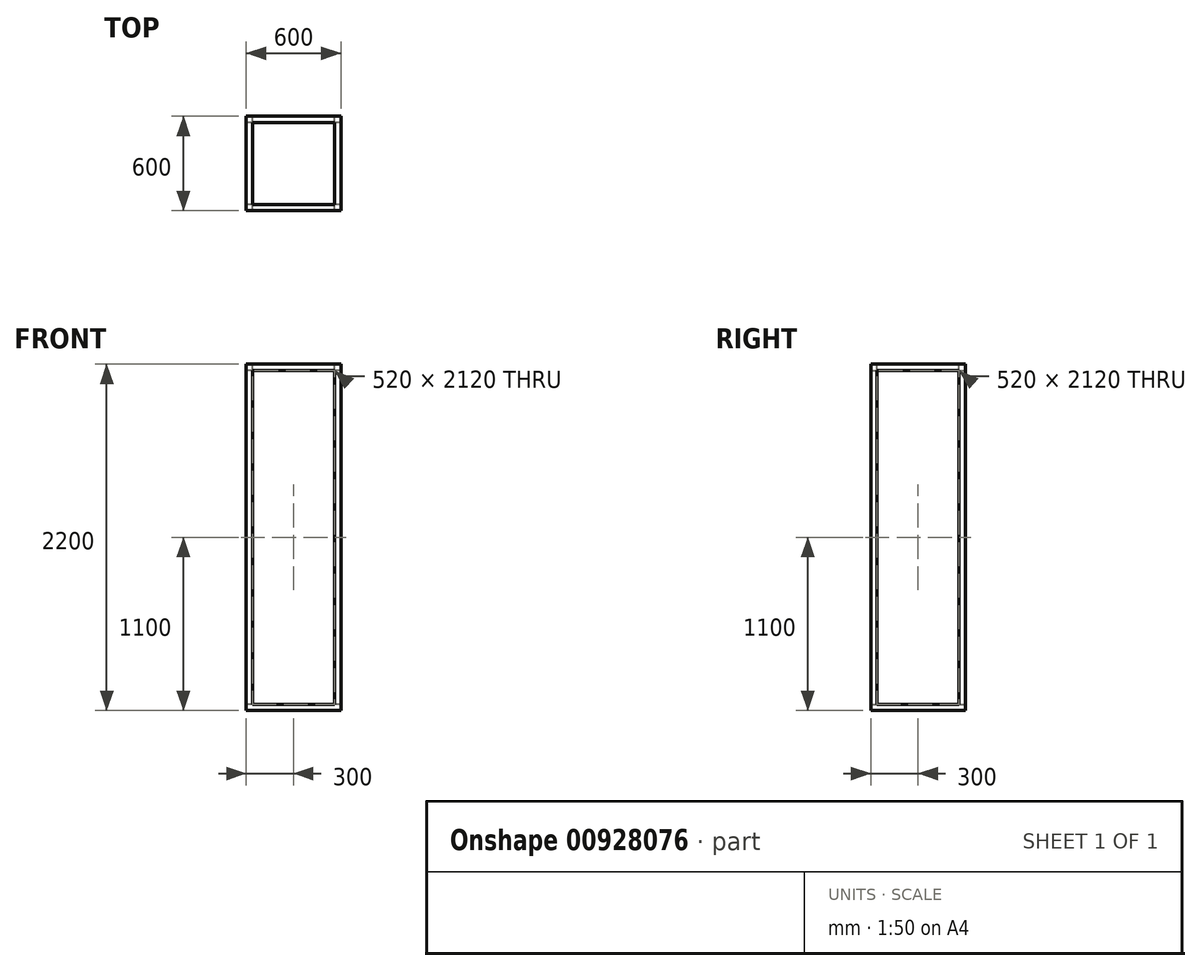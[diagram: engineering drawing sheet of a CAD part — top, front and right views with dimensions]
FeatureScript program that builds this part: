
annotation { "Feature Type Name" : "Feature", "Feature Type Description" : "" }
export const myFeature = defineFeature(function(context is Context, id is Id, definition is map)
    precondition{}
    {
        {
            var Q0;
            Q0=qCreatedBy(makeId("Right.planeOp"),FACE);
            var sketch = newSketch(context, id + "F0", { "sketchPlane" : qUnion([Q0])});
            skLineSegment(sketch, "E0.bottom", {"start": v(-260, -1060) * mm, "end": v(260, -1060) * mm});
            skLineSegment(sketch, "E0.top", {"start": v(-260, 1060) * mm, "end": v(260, 1060) * mm});
            skLineSegment(sketch, "E0.left", {"start": v(-260, -1060) * mm, "end": v(-260, 1060) * mm});
            skLineSegment(sketch, "E0.right", {"start": v(260, -1060) * mm, "end": v(260, 1060) * mm});
            skPoint(sketch, "E0.middle", {"position": v(0, 0) * mm});
            skLineSegment(sketch, "E1.bottom", {"start": v(-300, -1100) * mm, "end": v(300, -1100) * mm});
            skLineSegment(sketch, "E1.top", {"start": v(-300, 1100) * mm, "end": v(300, 1100) * mm});
            skLineSegment(sketch, "E1.left", {"start": v(-300, -1100) * mm, "end": v(-300, 1100) * mm});
            skLineSegment(sketch, "E1.right", {"start": v(300, -1100) * mm, "end": v(300, 1100) * mm});
            skSolve(sketch);
        }
        {
            var Q0;
            Q0=makeQuery(id+"F0.imprint","IMPRINT",FACE,{"disambiguationData":[TD([[makeQuery(id+"F0.imprint","IMPRINT",EDGE,{"derivedFrom":sQuery(id+"F0.wireOp",EDGE,"E0.bottom")}),-1.0]])]});
            extrude(context, id + "F1", {"entities" : qUnion([Q0]), "depth" : 600 * mm, "offsetDistance" : 25 * mm});
        }
        {
            var Q0;
            Q0=makeQuery(id+"F1.opExtrude","SWEPT_FACE",FACE,{"disambiguationData":[OSD([sQuery(id+"F0.wireOp",EDGE,"E1.top")])]});
            var sketch = newSketch(context, id + "F2", { "sketchPlane" : qUnion([Q0])});
            skLineSegment(sketch, "E2.bottom", {"start": v(560, -260) * mm, "end": v(40, -260) * mm});
            skLineSegment(sketch, "E2.top", {"start": v(560, 260) * mm, "end": v(40, 260) * mm});
            skLineSegment(sketch, "E2.left", {"start": v(560, -260) * mm, "end": v(560, 260) * mm});
            skLineSegment(sketch, "E2.right", {"start": v(40, -260) * mm, "end": v(40, 260) * mm});
            skPoint(sketch, "E2.middle", {"position": v(300, 0) * mm});
            skPoint(sketch, "E2.middle.positionSnap0", {"position": v(300, -300) * mm});
            skPoint(sketch, "E2.centerSnap0", {"position": v(300, -300) * mm});
            skSolve(sketch);
        }
        {
            var Q0;
            Q0=makeQuery(id+"F2.imprint","IMPRINT",FACE,{"disambiguationData":[TD([[makeQuery(id+"F2.imprint","IMPRINT",EDGE,{"derivedFrom":sQuery(id+"F2.wireOp",EDGE,"E2.bottom")}),-1.0]])]});
            extrude(context, id + "F3", {"entities" : qUnion([Q0]), "operationType" : NewBodyOperationType.REMOVE, "endBound" : BoundingType.UP_TO_NEXT, "oppositeDirection" : true, "depth" : 25 * mm, "offsetDistance" : 25 * mm});
        }
        {
            var Q0;
            Q0=makeQuery(id+"F1.opExtrude","SWEPT_FACE",FACE,{"disambiguationData":[OSD([sQuery(id+"F0.wireOp",EDGE,"E1.right")])]});
            var sketch = newSketch(context, id + "F4", { "sketchPlane" : qUnion([Q0])});
            skLineSegment(sketch, "E3.bottom", {"start": v(-560, -1060) * mm, "end": v(-40, -1060) * mm});
            skLineSegment(sketch, "E3.top", {"start": v(-560, 1060) * mm, "end": v(-40, 1060) * mm});
            skLineSegment(sketch, "E3.left", {"start": v(-560, -1060) * mm, "end": v(-560, 1060) * mm});
            skLineSegment(sketch, "E3.right", {"start": v(-40, -1060) * mm, "end": v(-40, 1060) * mm});
            skPoint(sketch, "E3.middle", {"position": v(-300, 0) * mm});
            skPoint(sketch, "E3.middle.positionSnap0", {"position": v(-300, -1100) * mm});
            skPoint(sketch, "E3.centerSnap0", {"position": v(-300, -1100) * mm});
            skSolve(sketch);
        }
        {
            var Q0;
            Q0=makeQuery(id+"F4.imprint","IMPRINT",FACE,{"disambiguationData":[TD([[makeQuery(id+"F4.imprint","IMPRINT",EDGE,{"derivedFrom":sQuery(id+"F4.wireOp",EDGE,"E3.bottom")}),1.0]])]});
            var Q1;
            Q1=makeQuery(id+"F1.opExtrude","SWEPT_FACE",FACE,{"disambiguationData":[OSD([sQuery(id+"F0.wireOp",EDGE,"E1.left")])]});
            extrude(context, id + "F5", {"entities" : qUnion([Q0]), "operationType" : NewBodyOperationType.REMOVE, "endBound" : BoundingType.UP_TO_SURFACE, "oppositeDirection" : true, "depth" : 25 * mm, "endBoundEntityFace" : qUnion([Q1]), "offsetDistance" : 25 * mm});
        }
    });
